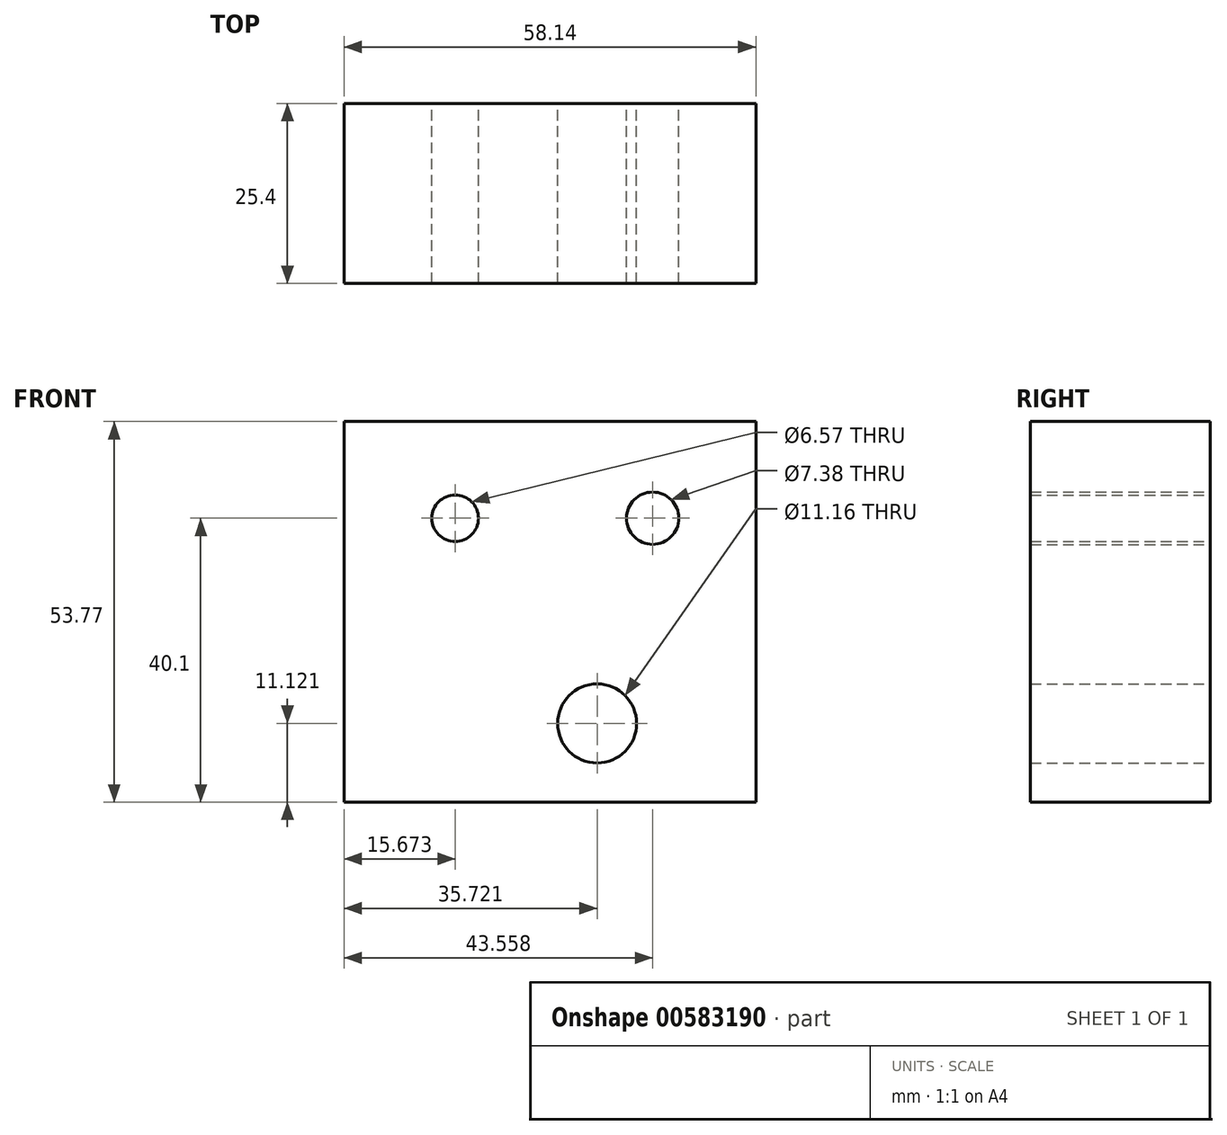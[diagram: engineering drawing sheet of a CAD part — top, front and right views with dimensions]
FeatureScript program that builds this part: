
annotation { "Feature Type Name" : "Feature", "Feature Type Description" : "" }
export const myFeature = defineFeature(function(context is Context, id is Id, definition is map)
    precondition{}
    {
        {
            var Q0;
            Q0=qCreatedBy(makeId("Front.planeOp"),FACE);
            var sketch = newSketch(context, id + "F0", { "sketchPlane" : qUnion([Q0])});
            skLineSegment(sketch, "E0.bottom", {"start": v(-28.34, 24.15) * mm, "end": v(29.8, 24.15) * mm});
            skLineSegment(sketch, "E0.top", {"start": v(-28.34, -29.62) * mm, "end": v(29.8, -29.62) * mm});
            skLineSegment(sketch, "E0.left", {"start": v(-28.34, 24.15) * mm, "end": v(-28.34, -29.62) * mm});
            skLineSegment(sketch, "E0.right", {"start": v(29.8, 24.15) * mm, "end": v(29.8, -29.62) * mm});
            skCircle(sketch, "E1", {"center": v(-12.67, 10.48) * mm, "radius": 3.29 * mm});
            skCircle(sketch, "E2", {"center": v(15.22, 10.48) * mm, "radius": 3.7 * mm});
            skCircle(sketch, "E3", {"center": v(7.38, -18.5) * mm, "radius": 5.58 * mm});
            skSolve(sketch);
        }
        {
            var Q0;
            Q0=makeQuery(id+"F0.imprint","IMPRINT",FACE,{"disambiguationData":[TD([[makeQuery(id+"F0.imprint","IMPRINT",EDGE,{"derivedFrom":sQuery(id+"F0.wireOp",EDGE,"E0.bottom")}),-1.0]])]});
            extrude(context, id + "F1", {"entities" : qUnion([Q0]), "depth" : 25.4 * mm, "offsetDistance" : 25.4 * mm});
        }
    });
